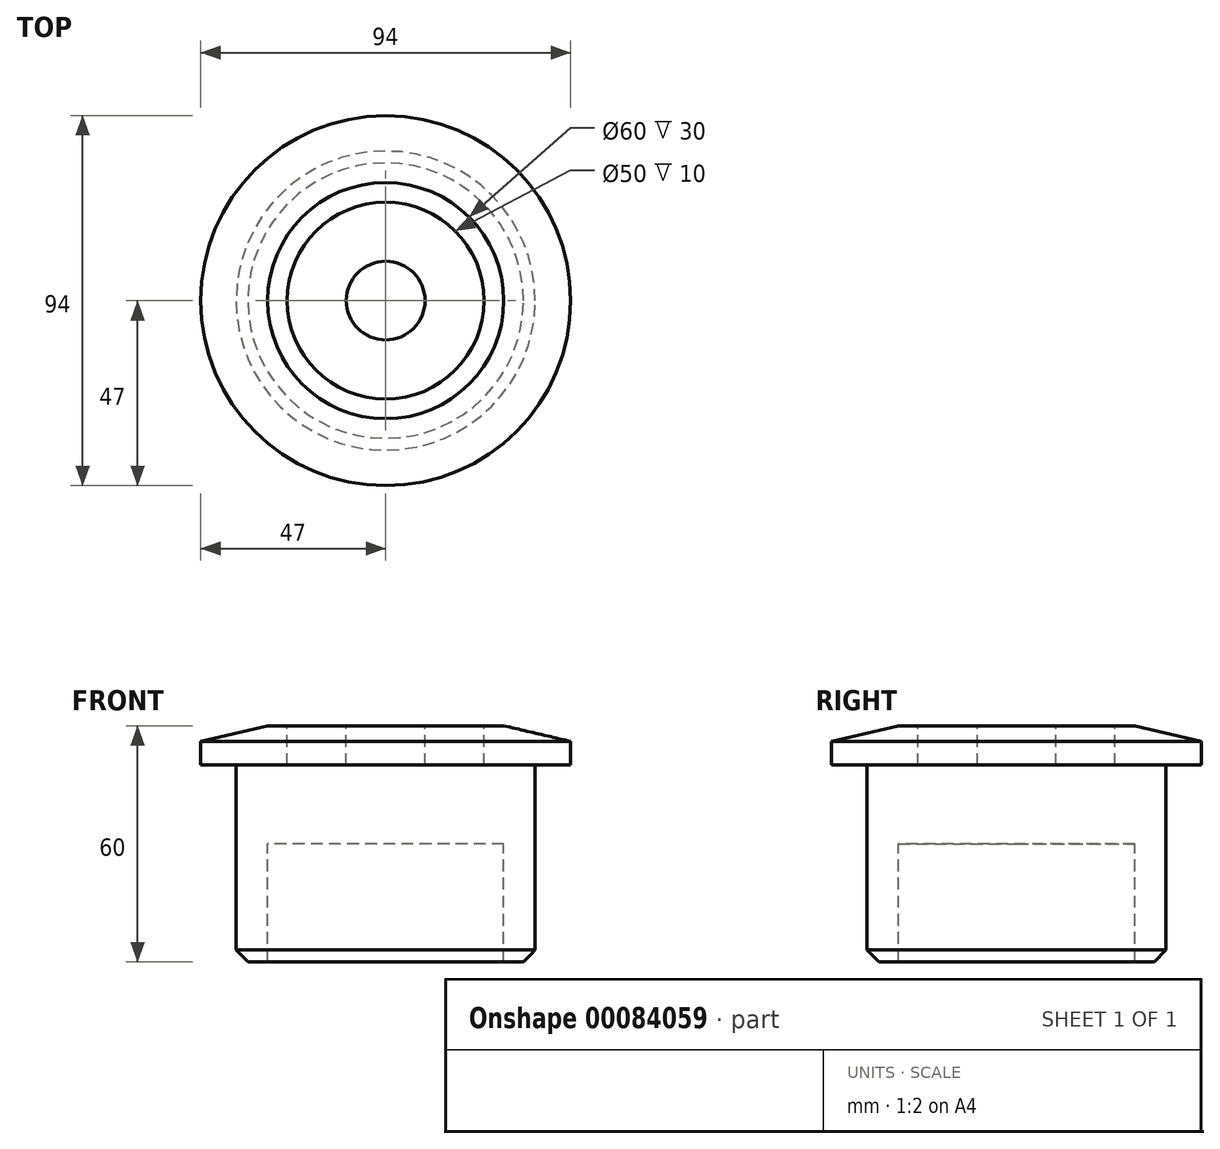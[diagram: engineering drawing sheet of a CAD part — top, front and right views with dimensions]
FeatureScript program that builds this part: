
annotation { "Feature Type Name" : "Feature", "Feature Type Description" : "" }
export const myFeature = defineFeature(function(context is Context, id is Id, definition is map)
    precondition{}
    {
        {
            var Q0;
            Q0=qCreatedBy(makeId("Front.planeOp"),FACE);
            var sketch = newSketch(context, id + "F0", { "sketchPlane" : qUnion([Q0])});
            skLineSegment(sketch, "E0", {"start": v(38, 50) * mm, "end": v(47, 50) * mm});
            skLineSegment(sketch, "E1", {"start": v(47, 50) * mm, "end": v(47, 56) * mm});
            skLineSegment(sketch, "E2", {"start": v(47, 56) * mm, "end": v(30, 60) * mm});
            skLineSegment(sketch, "E3", {"start": v(0, 60) * mm, "end": v(0, 0) * mm});
            skLineSegment(sketch, "E4", {"start": v(30, 0) * mm, "end": v(30, 30) * mm});
            skLineSegment(sketch, "E5", {"start": v(30, 30) * mm, "end": v(0, 30) * mm});
            skLineSegment(sketch, "E6", {"start": v(35, 0) * mm, "end": v(38, 3) * mm});
            skLineSegment(sketch, "E7", {"start": v(0, 0) * mm, "end": v(35, 0) * mm});
            skLineSegment(sketch, "E8", {"start": v(38, 3) * mm, "end": v(38, 50) * mm});
            skLineSegment(sketch, "E9", {"start": v(0, 60) * mm, "end": v(10, 60) * mm});
            skLineSegment(sketch, "E10", {"start": v(10, 60) * mm, "end": v(10, 50) * mm});
            skLineSegment(sketch, "E11", {"start": v(30, 60) * mm, "end": v(25, 60) * mm});
            skLineSegment(sketch, "E12", {"start": v(25, 60) * mm, "end": v(25, 50) * mm});
            skLineSegment(sketch, "E13", {"start": v(25, 50) * mm, "end": v(10, 50) * mm});
            skSolve(sketch);
        }
        {
            var Q0;
            Q0=makeQuery(id+"F0.imprint","IMPRINT",FACE,{"disambiguationData":[TD([[makeQuery(id+"F0.imprint","IMPRINT",EDGE,{"derivedFrom":sQuery(id+"F0.wireOp",EDGE,"E0")}),1.0]])]});
            var Q1;
            Q1=sQuery(id+"F0.wireOp",EDGE,"E3");
            revolve(context, id + "F1", {"entities" : qUnion([Q0]), "axis" : qUnion([Q1]), "revolveType" : RevolveType.FULL});
        }
    });
